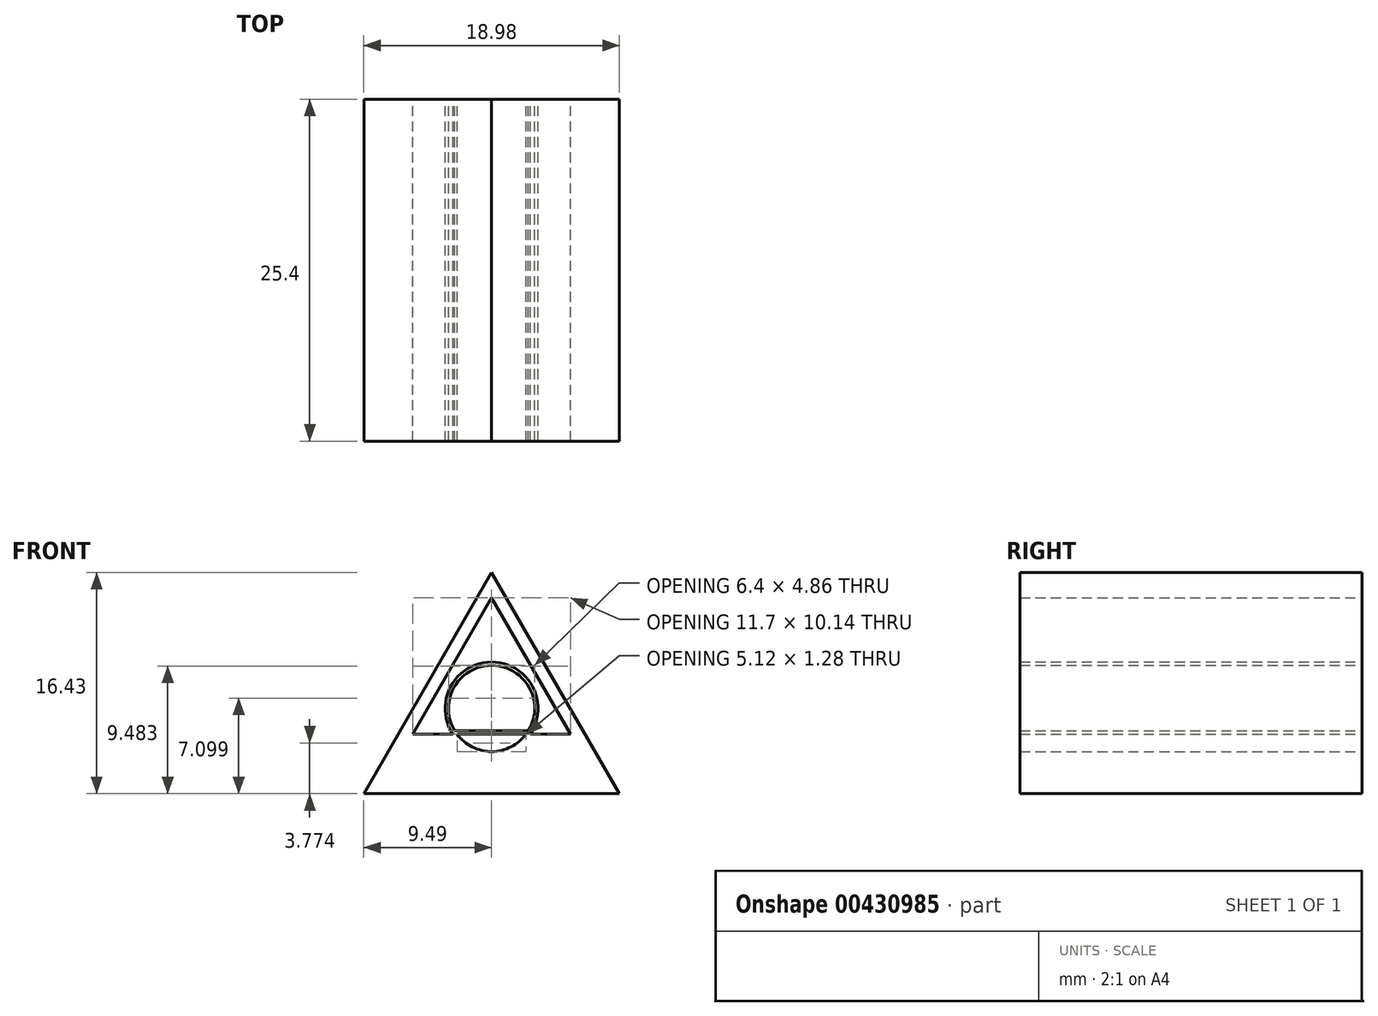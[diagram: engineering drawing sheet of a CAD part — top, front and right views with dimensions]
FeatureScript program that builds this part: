
annotation { "Feature Type Name" : "Feature", "Feature Type Description" : "" }
export const myFeature = defineFeature(function(context is Context, id is Id, definition is map)
    precondition{}
    {
        {
            var Q0;
            Q0=qCreatedBy(makeId("Front.planeOp"),FACE);
            var sketch = newSketch(context, id + "F0", { "sketchPlane" : qUnion([Q0])});
            skCircle(sketch, "E0", {"center": v(0, 0) * mm, "radius": 3.2 * mm});
            skCircle(sketch, "E1", {"center": v(0, 0) * mm, "radius": 3.45 * mm});
            skLineSegment(sketch, "E2", {"start": v(0, 8.22) * mm, "end": v(-7.86, -5.4) * mm});
            skLineSegment(sketch, "E3", {"start": v(-7.86, -5.4) * mm, "end": v(7.86, -5.4) * mm});
            skLineSegment(sketch, "E4", {"start": v(7.86, -5.4) * mm, "end": v(0, 8.22) * mm});
            skLineSegment(sketch, "E5.bottom", {"start": v(-6.28, -1.66) * mm, "end": v(6.58, -1.66) * mm});
            skLineSegment(sketch, "E5.top", {"start": v(-6.28, -1.91) * mm, "end": v(6.58, -1.91) * mm});
            skLineSegment(sketch, "E5.left", {"start": v(-6.28, -1.66) * mm, "end": v(-6.28, -1.91) * mm});
            skLineSegment(sketch, "E5.right", {"start": v(6.58, -1.66) * mm, "end": v(6.58, -1.91) * mm});
            skLineSegment(sketch, "E6.0", {"start": v(0, 10.1) * mm, "end": v(-9.49, -6.33) * mm});
            skLineSegment(sketch, "E6.1", {"start": v(9.49, -6.33) * mm, "end": v(0, 10.1) * mm});
            skLineSegment(sketch, "E6.2", {"start": v(-9.49, -6.33) * mm, "end": v(9.49, -6.33) * mm});
            skSolve(sketch);
        }
        {
            var Q0;
            {var subQ0=sQuery(id+"F0.wireOp",EDGE,"E5.bottom");var subQ1=sQuery(id+"F0.wireOp",EDGE,"E0");var subQ2=makeQuery(id+"F0.imprint","INTERSECT",VERTEX,{"disambiguationData":[OD(0.0)],"derivedFrom":[subQ1,subQ0]});Q0=makeQuery(id+"F0.imprint","IMPRINT",FACE,{"disambiguationData":[TD([[makeQuery(id+"F0.imprint","IMPRINT",EDGE,{"disambiguationData":[TD([[subQ2,1.0]])],"derivedFrom":subQ1}),-1.0]])]});}
            var Q1;
            {var subQ0=sQuery(id+"F0.wireOp",EDGE,"E5.top");var subQ1=sQuery(id+"F0.wireOp",EDGE,"E0");var subQ2=makeQuery(id+"F0.imprint","INTERSECT",VERTEX,{"disambiguationData":[OD(0.0)],"derivedFrom":[subQ1,subQ0]});Q1=makeQuery(id+"F0.imprint","IMPRINT",FACE,{"disambiguationData":[TD([[makeQuery(id+"F0.imprint","IMPRINT",EDGE,{"disambiguationData":[TD([[subQ2,-1.0]])],"derivedFrom":subQ1}),-1.0]])]});}
            var Q2;
            {var subQ0=sQuery(id+"F0.wireOp",EDGE,"E5.top");var subQ1=sQuery(id+"F0.wireOp",EDGE,"E0");var subQ2=makeQuery(id+"F0.imprint","INTERSECT",VERTEX,{"disambiguationData":[OD(0.0)],"derivedFrom":[subQ1,subQ0]});Q2=makeQuery(id+"F0.imprint","IMPRINT",FACE,{"disambiguationData":[TD([[makeQuery(id+"F0.imprint","IMPRINT",EDGE,{"disambiguationData":[TD([[subQ2,1.0]])],"derivedFrom":subQ1}),1.0]])]});}
            var Q3;
            {var subQ0=sQuery(id+"F0.wireOp",EDGE,"E5.top");var subQ1=sQuery(id+"F0.wireOp",EDGE,"E0");var subQ2=makeQuery(id+"F0.imprint","INTERSECT",VERTEX,{"disambiguationData":[OD(0.0)],"derivedFrom":[subQ1,subQ0]});Q3=makeQuery(id+"F0.imprint","IMPRINT",FACE,{"disambiguationData":[TD([[makeQuery(id+"F0.imprint","IMPRINT",EDGE,{"disambiguationData":[TD([[subQ2,1.0]])],"derivedFrom":subQ1}),-1.0]])]});}
            var Q4;
            {var subQ0=sQuery(id+"F0.wireOp",EDGE,"E5.top");var subQ1=sQuery(id+"F0.wireOp",EDGE,"E1");var subQ2=makeQuery(id+"F0.imprint","INTERSECT",VERTEX,{"disambiguationData":[OD(0.0)],"derivedFrom":[subQ1,subQ0]});Q4=makeQuery(id+"F0.imprint","IMPRINT",FACE,{"disambiguationData":[TD([[makeQuery(id+"F0.imprint","IMPRINT",EDGE,{"disambiguationData":[TD([[subQ2,1.0]])],"derivedFrom":subQ1}),-1.0]])]});}
            var Q5;
            {var subQ0=sQuery(id+"F0.wireOp",EDGE,"E5.top");var subQ1=sQuery(id+"F0.wireOp",EDGE,"E1");var subQ2=makeQuery(id+"F0.imprint","INTERSECT",VERTEX,{"disambiguationData":[OD(1.0)],"derivedFrom":[subQ1,subQ0]});Q5=makeQuery(id+"F0.imprint","IMPRINT",FACE,{"disambiguationData":[TD([[makeQuery(id+"F0.imprint","IMPRINT",EDGE,{"disambiguationData":[TD([[subQ2,-1.0]])],"derivedFrom":subQ1}),-1.0]])]});}
            var Q6;
            {var subQ0=sQuery(id+"F0.wireOp",EDGE,"E5.top");var subQ1=sQuery(id+"F0.wireOp",EDGE,"E0");var subQ2=makeQuery(id+"F0.imprint","INTERSECT",VERTEX,{"disambiguationData":[OD(1.0)],"derivedFrom":[subQ1,subQ0]});Q6=makeQuery(id+"F0.imprint","IMPRINT",FACE,{"disambiguationData":[TD([[makeQuery(id+"F0.imprint","IMPRINT",EDGE,{"disambiguationData":[TD([[subQ2,-1.0]])],"derivedFrom":subQ1}),-1.0]])]});}
            var Q7;
            {var subQ10=sQuery(id+"F0.wireOp",EDGE,"E3");Q7=makeQuery(id+"F0.imprint","IMPRINT",FACE,{"disambiguationData":[TD([[makeQuery(id+"F0.imprint","IMPRINT",EDGE,{"derivedFrom":subQ10}),-1.0]])]});}
            var Q8;
            {var subQ5=sQuery(id+"F0.wireOp",EDGE,"E5.right");Q8=makeQuery(id+"F0.imprint","IMPRINT",FACE,{"disambiguationData":[TD([[makeQuery(id+"F0.imprint","IMPRINT",EDGE,{"derivedFrom":subQ5}),-1.0]])]});}
            var Q9;
            {var subQ5=sQuery(id+"F0.wireOp",EDGE,"E5.left");Q9=makeQuery(id+"F0.imprint","IMPRINT",FACE,{"disambiguationData":[TD([[makeQuery(id+"F0.imprint","IMPRINT",EDGE,{"derivedFrom":subQ5}),1.0]])]});}
            extrude(context, id + "F1", {"entities" : qUnion([Q0, Q1, Q2, Q3, Q4, Q5, Q6, Q7, Q8, Q9]), "depth" : 25.4 * mm});
        }
    });
